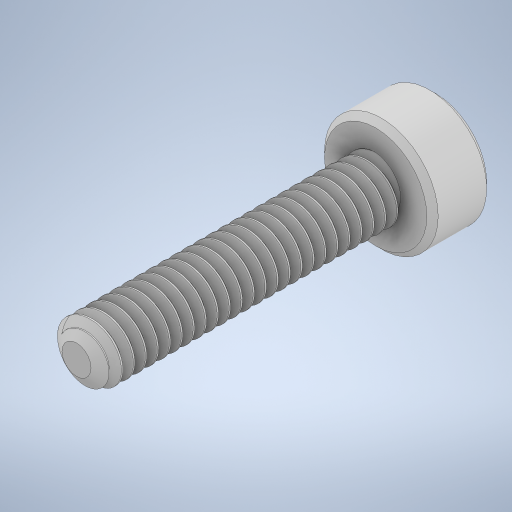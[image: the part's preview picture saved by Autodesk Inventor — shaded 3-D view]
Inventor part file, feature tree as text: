
AUTODESK INVENTOR PART (.ipt)
format: ipt  version: 2024 (Build 280153000, 153)  size: 902,144 bytes
history: native  units: mm
features: other x1, chamfer x1
ambient origin geometry x8: Origin, YZ Plane, XZ Plane, XY Plane, X Axis, Y Axis, Z Axis, Center Point
bodies: Body1 (feature_tree)
feature tree (2):
  other  "Těleso1"
  chamfer  "Chamfer1"  [1 undecoded]
note: 1 required parameter value undecoded (feature->parameter linkage not recoverable at this tier; creation-order binding heuristic only, values carry confidence <= 0.55)
